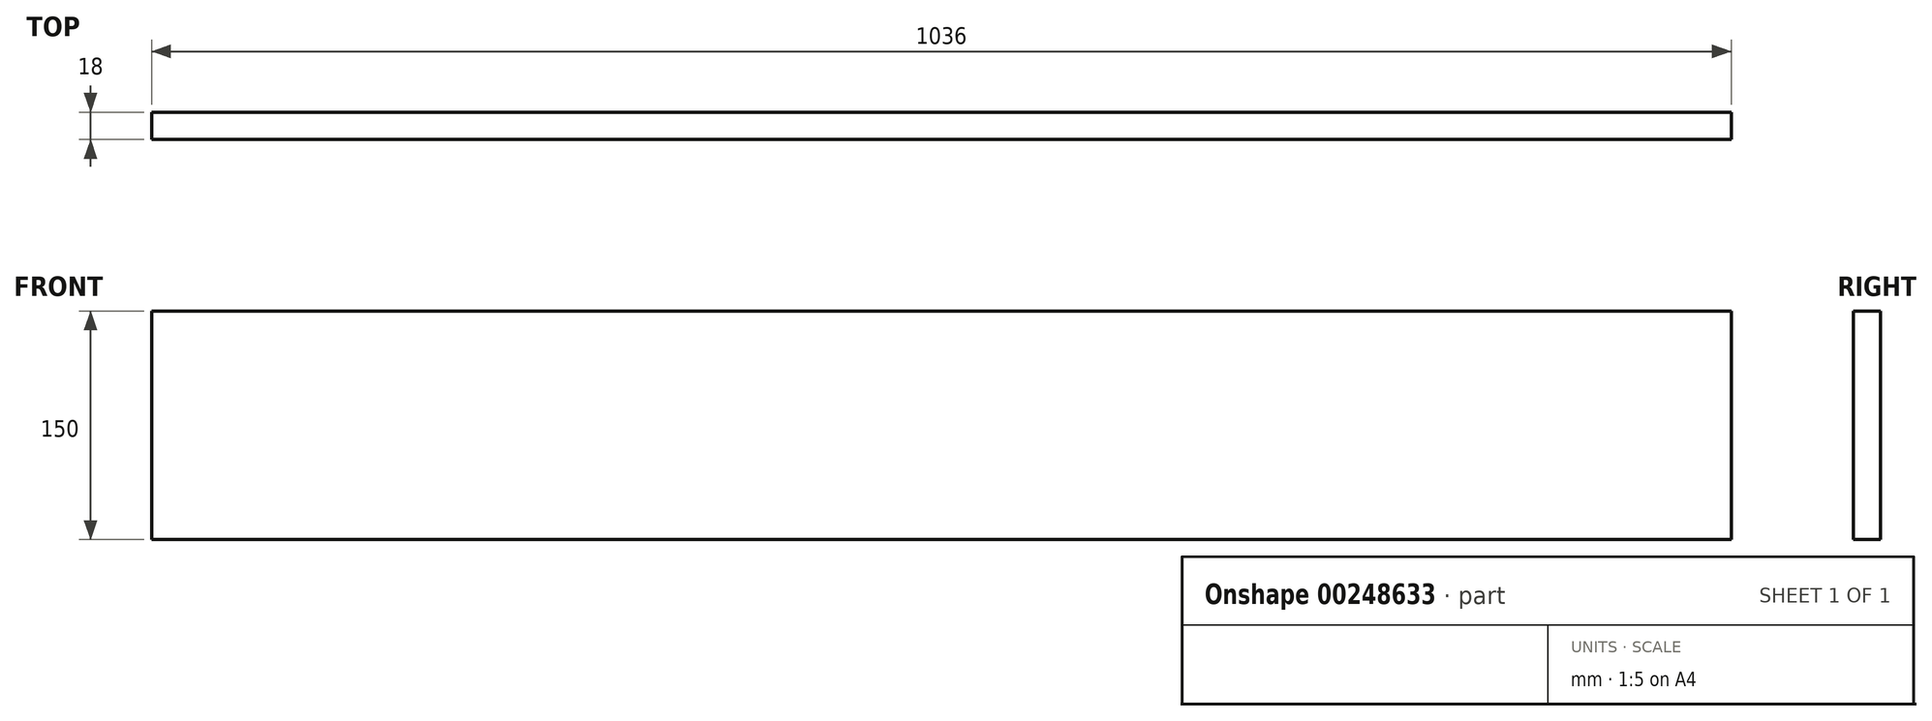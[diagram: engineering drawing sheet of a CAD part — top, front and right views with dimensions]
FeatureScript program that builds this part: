
annotation { "Feature Type Name" : "Feature", "Feature Type Description" : "" }
export const myFeature = defineFeature(function(context is Context, id is Id, definition is map)
    precondition{}
    {
        {
            var Q0;
            Q0=qCreatedBy(makeId("Front.planeOp"),FACE);
            var sketch = newSketch(context, id + "F0", { "sketchPlane" : qUnion([Q0])});
            skLineSegment(sketch, "E0.bottom", {"start": v(-419.06, 150) * mm, "end": v(616.94, 150) * mm});
            skLineSegment(sketch, "E0.top", {"start": v(-419.06, 0) * mm, "end": v(616.94, 0) * mm});
            skLineSegment(sketch, "E0.left", {"start": v(-419.06, 150) * mm, "end": v(-419.06, 0) * mm});
            skLineSegment(sketch, "E0.right", {"start": v(616.94, 150) * mm, "end": v(616.94, 0) * mm});
            skSolve(sketch);
        }
        {
            var Q0;
            Q0 = qSketchRegion(id + "F0", true);
            extrude(context, id + "F1", {"entities" : qUnion([Q0]), "depth" : 18 * mm});
        }
    });
